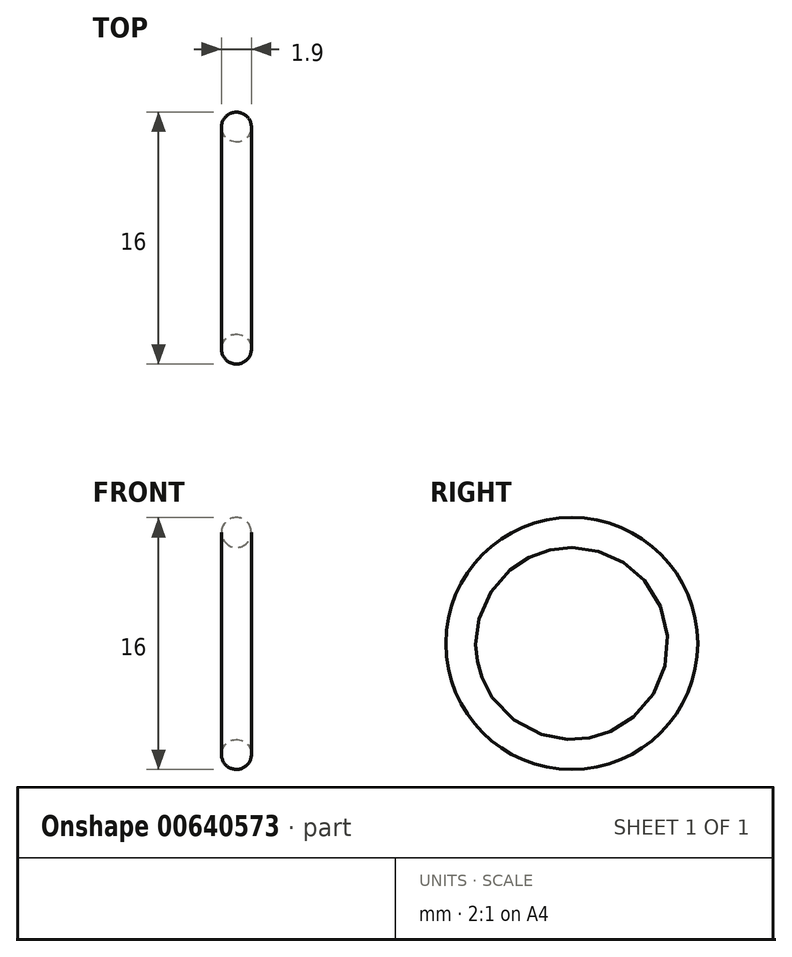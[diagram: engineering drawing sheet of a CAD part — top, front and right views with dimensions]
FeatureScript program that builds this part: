
annotation { "Feature Type Name" : "Feature", "Feature Type Description" : "" }
export const myFeature = defineFeature(function(context is Context, id is Id, definition is map)
    precondition{}
    {
        {
            var Q0;
            Q0=qCreatedBy(makeId("Front.planeOp"),FACE);
            var sketch = newSketch(context, id + "F0", { "sketchPlane" : qUnion([Q0])});
            skCircle(sketch, "E0", {"center": v(0.95, 7.05) * mm, "radius": 0.95 * mm});
            skLineSegment(sketch, "E1", {"start": v(-8.69, 0) * mm, "end": v(12.4, 0) * mm, "construction": true});
            skLineSegment(sketch, "E2", {"start": v(0, 0) * mm, "end": v(0, 18.56) * mm, "construction": true});
            skSolve(sketch);
        }
        {
            var Q0;
            Q0 = qSketchRegion(id + "F0", true);
            var Q1;
            Q1=sQuery(id+"F0.wireOp",EDGE,"E1");
            revolve(context, id + "F1", {"entities" : qUnion([Q0]), "axis" : qUnion([Q1]), "revolveType" : RevolveType.FULL});
        }
    });
